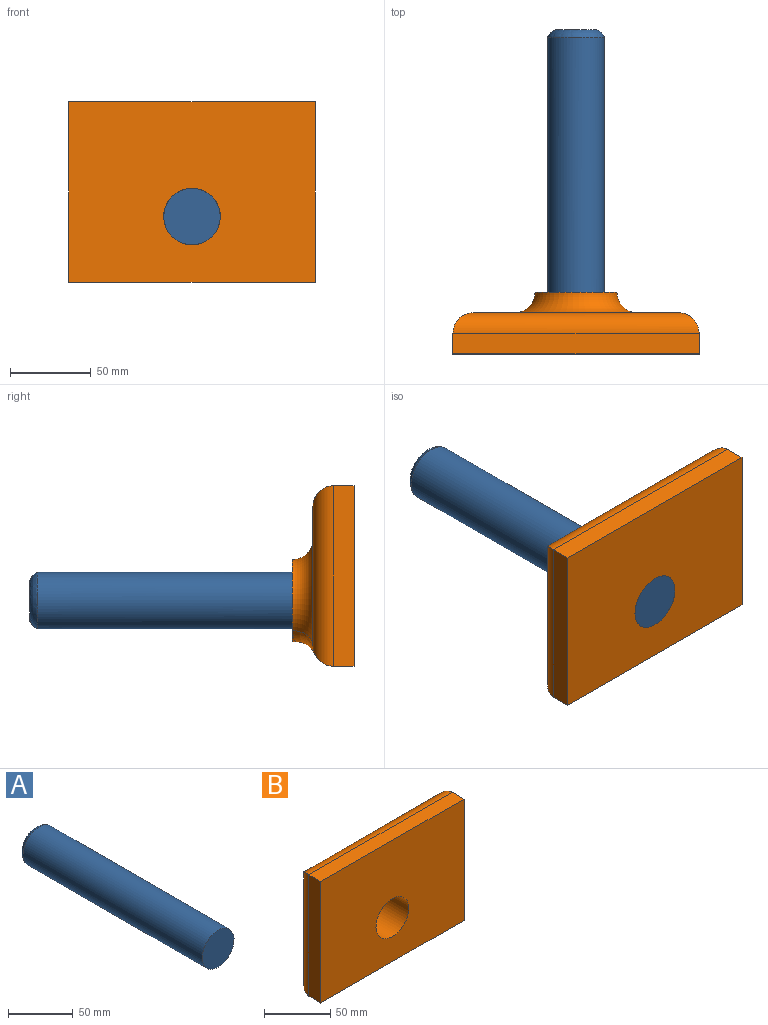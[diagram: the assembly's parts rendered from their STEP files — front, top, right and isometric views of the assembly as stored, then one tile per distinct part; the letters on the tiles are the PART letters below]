
ASSEMBLY  parts=2 mates=1
PART A: 4 faces, bbox 34.9x200.7x34.9 mm
  f0: cylinder r=17.46mm len=195.88mm, axis (0,-1,0), area 21492.5mm2, adj f2,f3
  f1: plane 25.38x25.38mm, normal (0,1,0), area 505.6mm2, adj f3
  f2: plane 34.93x34.93mm, normal (0,-1,0), area 958mm2, adj f0
  f3: bspline ~34.93x34.93mm, area 691.3mm2, adj f0,f1
PART B: 15 faces, bbox 152.4x47.1x111.8 mm
  f0: plane 111.76x12.7mm, normal (1,0,0), area 1419.4mm2, adj f1,f3,f4,f9
  f1: plane 152.4x12.7mm, normal (0,0,-1), area 1935.5mm2, adj f0,f2,f4,f11
  f2: plane 111.76x12.7mm, normal (-1,0,0), area 1419.4mm2, adj f1,f3,f4,f10
  f3: plane 152.4x12.7mm, normal (0,0,1), area 1935.5mm2, adj f0,f2,f4,f8
  f4: plane 152.4x111.76mm, normal (0,-1,0), area 16067.3mm2, adj f0,f1,f2,f3,f14
  f5: plane 127x86.36mm, normal (0,1,0), area 6768.8mm2, adj f8,f9,f10,f11,f12
  f6: cylinder r=25.4mm len=34.54mm, axis (0,1,0), area 41.9mm2, adj f7,f13
  f7: plane 50.8x50.8mm, normal (0,1,0), area 1061.9mm2, adj f6,f12,f14
  f8: cylinder r=12.7mm len=152.4mm, axis (-1,0,0), area 2856.1mm2, adj f3,f5,f9,f10
  f9: cylinder r=12.7mm len=111.76mm, axis (0,0,1), area 2045.4mm2, adj f0,f5,f8,f11
  f10: cylinder r=12.7mm len=111.76mm, axis (0,0,-1), area 2045.4mm2, adj f2,f5,f8,f11
  f11: cylinder r=12.7mm len=152.4mm, axis (1,0,0), area 2671.8mm2, adj f1,f5,f9,f10,f13
  f12: torus R=38.1mm, axis (0,1,0), area 2866.9mm2, adj f5,f7,f13
  f13: bspline ~54.46x15.8mm, area 714.3mm2, adj f6,f11,f12
  f14: cylinder r=17.53mm len=38.1mm, axis (0,1,0), area 4195.5mm2, adj f4,f7
PLACE A at identity
PLACE B at identity
MATE fastened B.f6 <-> A.f0  axis (0,-1,0) through (0,0,-15.24)mm
